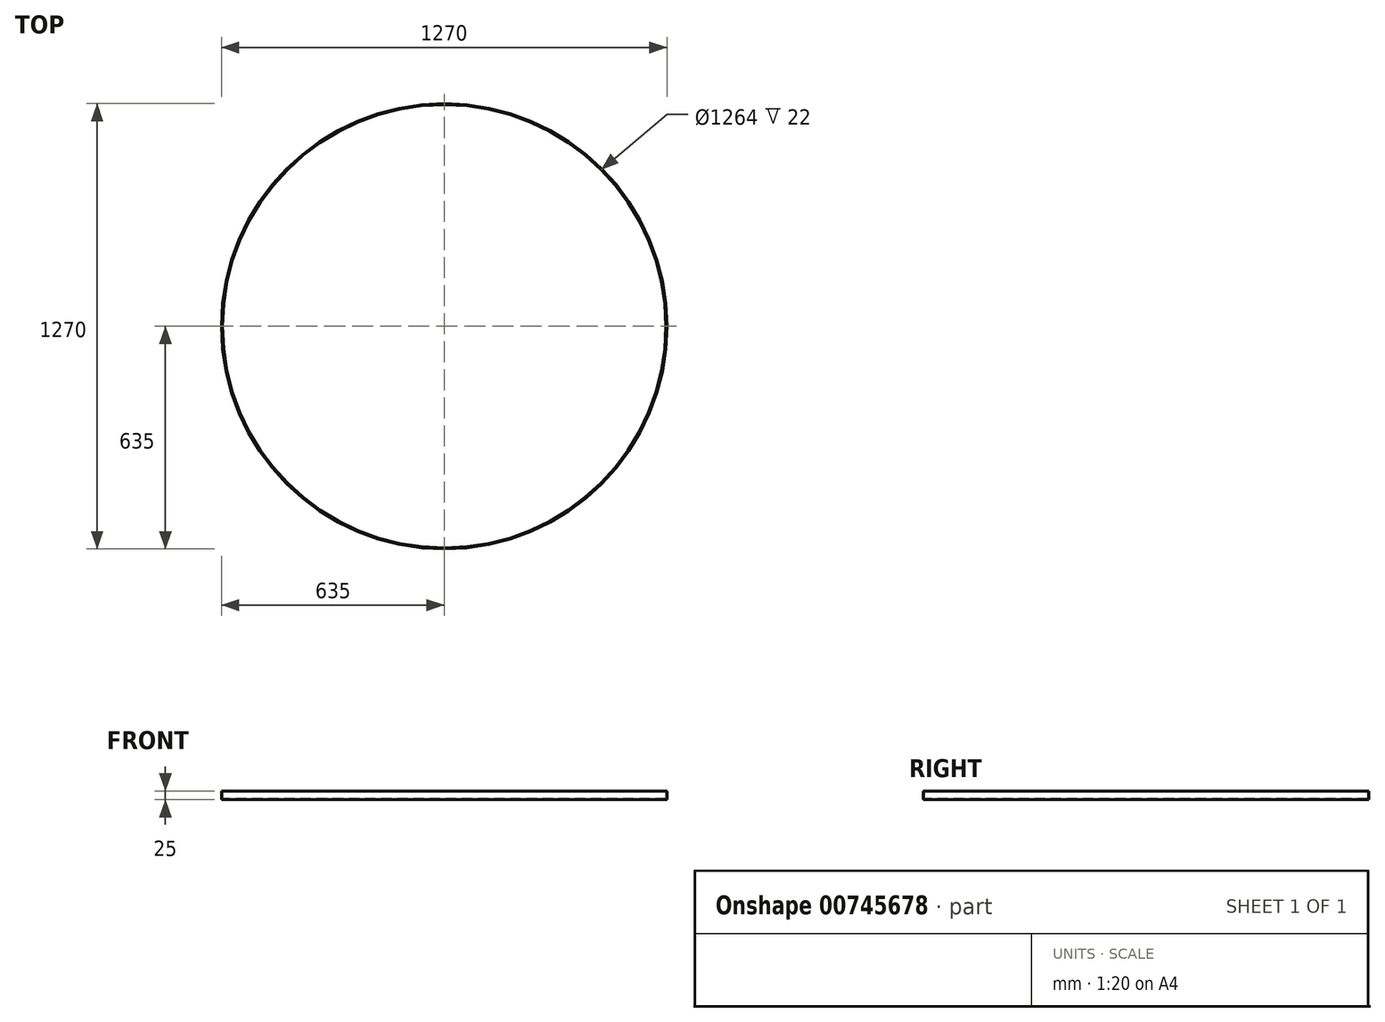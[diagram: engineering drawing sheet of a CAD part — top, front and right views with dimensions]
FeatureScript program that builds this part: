
annotation { "Feature Type Name" : "Feature", "Feature Type Description" : "" }
export const myFeature = defineFeature(function(context is Context, id is Id, definition is map)
    precondition{}
    {
        {
            assignVariable(context, id + "F0", {"name" : "base_h", "anyValue" : 25});
        }
        {
            assignVariable(context, id + "F1", {"name" : "shell_thickness", "anyValue" : 3});
        }
        {
            var Q0;
            Q0=qCreatedBy(makeId("Top.planeOp"),FACE);
            var sketch = newSketch(context, id + "F2", { "sketchPlane" : qUnion([Q0])});
            skCircle(sketch, "E0", {"center": v(0, 0) * mm, "radius": 635 * mm});
            skSolve(sketch);
        }
        {
            var Q0;
            Q0 = qSketchRegion(id + "F2", true);
            extrude(context, id + "F3", {"entities" : qUnion([Q0]), "depth" : (getVariable(context, 'base_h')) * mm, "offsetDistance" : 25.4 * mm});
        }
        {
            var Q0;
            Q0=makeQuery(id+"F3.opExtrude","CAP_FACE",FACE,{"disambiguationData":[OSD([sQuery(id+"F2.wireOp",EDGE,"E0")])],"isStart":false});
            shell(context, id + "F4", {"entities" : qUnion([Q0]), "thickness" : (getVariable(context, 'shell_thickness')) * mm});
        }
    });
